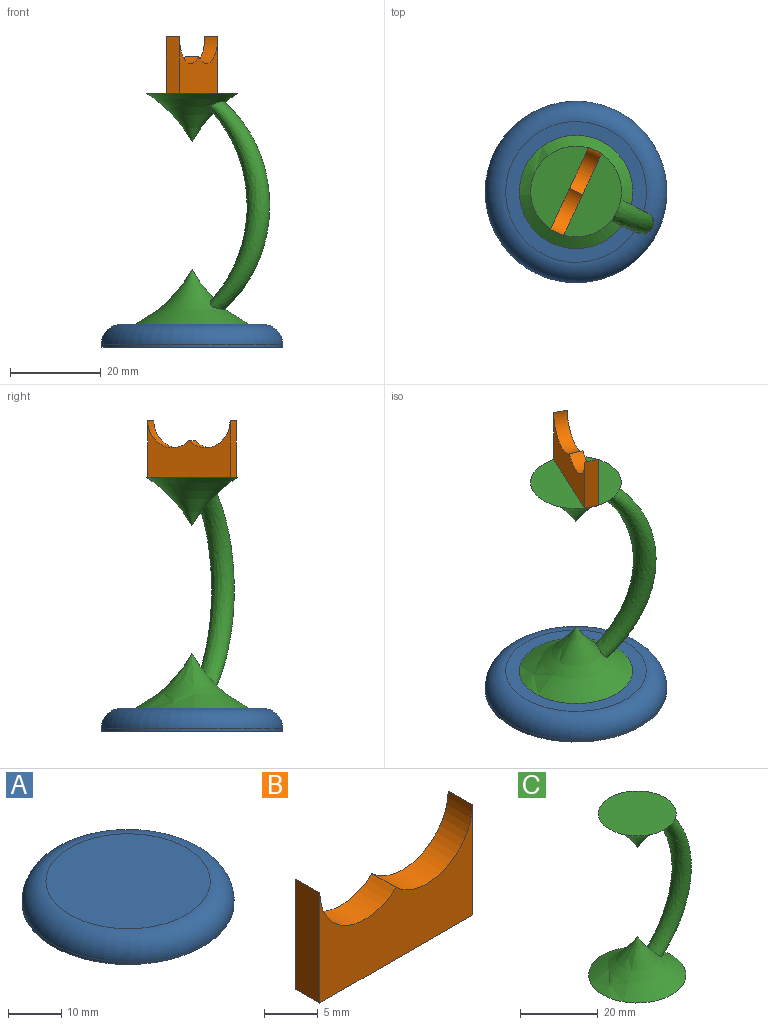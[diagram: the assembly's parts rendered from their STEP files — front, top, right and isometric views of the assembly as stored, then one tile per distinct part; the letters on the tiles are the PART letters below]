
ASSEMBLY  parts=3 mates=2
PART A: 4 faces, bbox 43.3x43.3x5.1 mm
  f0: cylinder r=20mm len=40mm, axis (0,0,-1), area 72.9mm2, adj f2,f3
  f1: plane 31x31mm, normal (0,0,1), area 754.8mm2, adj f3
  f2: plane 40x40mm, normal (0,0,-1), area 1256.6mm2, adj f0
  f3: torus R=15.5mm, axis (0,0,1), area 815.6mm2, adj f0,f1
PART B: 7 faces, bbox 20x3.2x12.5 mm
  f0: cylinder r=5.96mm len=10mm, axis (0,1,0), area 43.8mm2, adj f1,f4,f5,f6
  f1: plane 12.5x3.18mm, normal (-1,0,0), area 39.7mm2, adj f0,f2,f5,f6
  f2: plane 20x3.18mm, normal (0,0,-1), area 63.5mm2, adj f1,f3,f5,f6
  f3: plane 12.5x3.18mm, normal (1,0,0), area 39.7mm2, adj f2,f4,f5,f6
  f4: cylinder r=5.96mm len=10mm, axis (0,1,0), area 43.8mm2, adj f0,f3,f5,f6
  f5: plane 20x12.5mm, normal (0,-1,0), area 150.1mm2, adj f0,f1,f2,f3,f4
  f6: plane 20x12.5mm, normal (0,1,0), area 150.1mm2, adj f0,f1,f2,f3,f4
PART C: 5 faces, bbox 31.3x25x58.4 mm
  f0: bspline ~50.8x21.32mm, area 737mm2, adj f1,f3
  f1: torus R=25.6mm, axis (0,0,-1), area 611.4mm2, adj f0,f2
  f2: plane 25x25mm, normal (0,0,-1), area 490.9mm2, adj f1
  f3: torus R=25.6mm, axis (0,0,-1), area 408.6mm2, adj f0,f4
  f4: plane 20x20mm, normal (0,0,1), area 314.2mm2, adj f3
PLACE A rot(axis=(0,0,-1),25deg) t=(-118.6,-15.74,52.04)mm
PLACE B rot(axis=(0,0,1),65deg) t=(-120.04,-15.07,107.92)mm
PLACE C rot(axis=(0,0,-1),25deg) t=(-118.6,-15.74,57.12)mm
MATE fastened C.f1 <-> B.f2  axis (0,0,1) through (-118.6,-15.74,107.92)mm
MATE fastened A.f0 <-> C.f1  axis (0,0,1) through (-118.6,-15.74,57.12)mm
